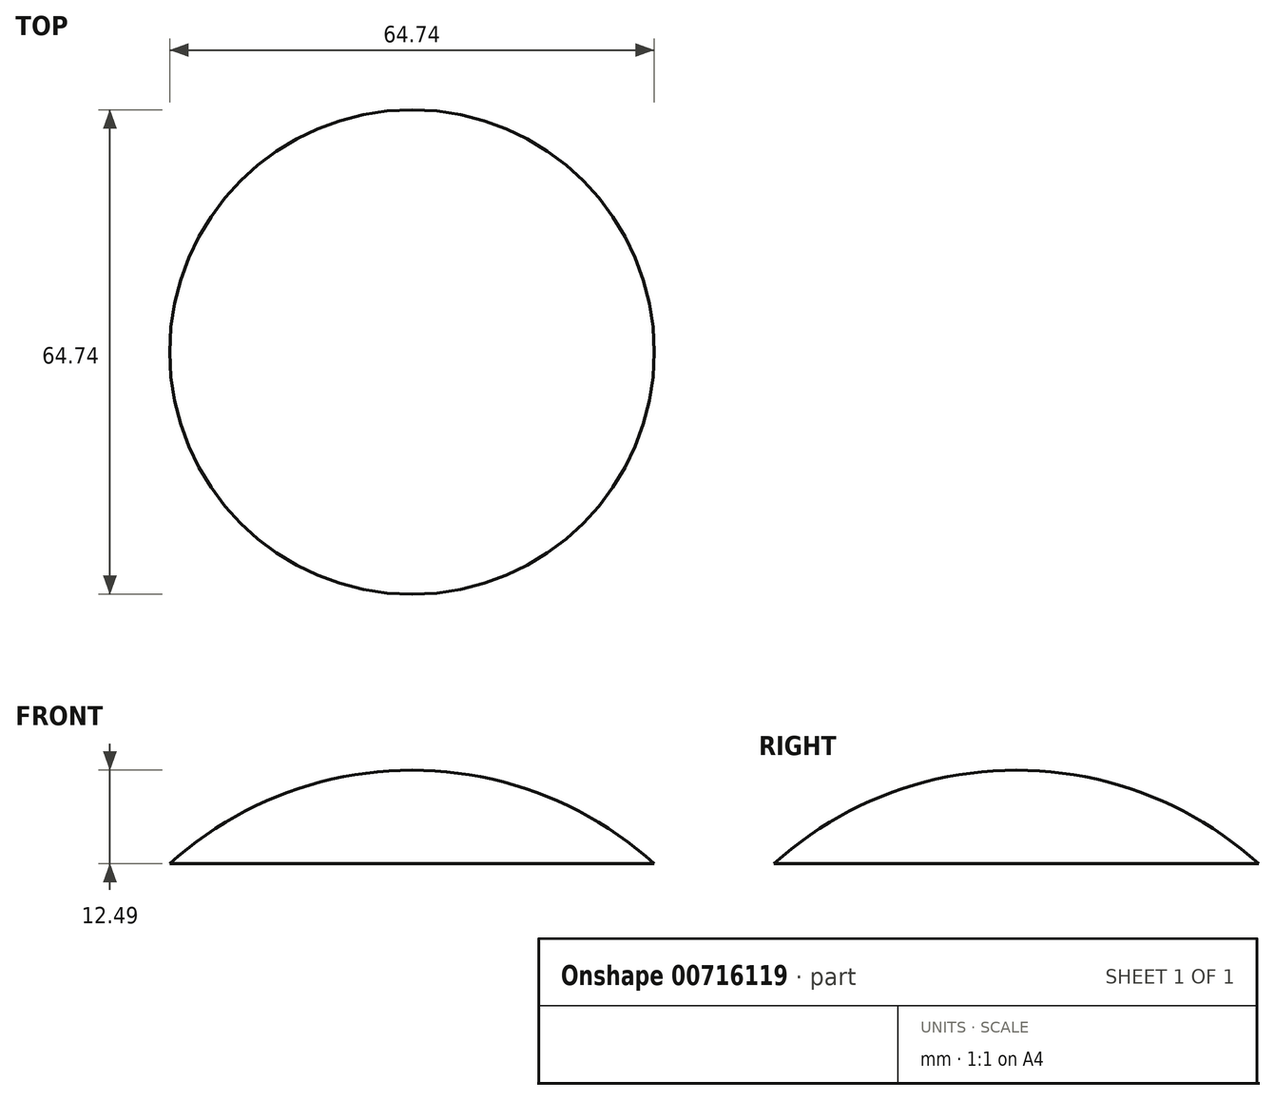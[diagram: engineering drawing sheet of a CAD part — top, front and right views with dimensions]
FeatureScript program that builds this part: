
annotation { "Feature Type Name" : "Feature", "Feature Type Description" : "" }
export const myFeature = defineFeature(function(context is Context, id is Id, definition is map)
    precondition{}
    {
        {
            var Q0;
            Q0=qCreatedBy(makeId("Front.planeOp"),FACE);
            var sketch = newSketch(context, id + "F0", { "sketchPlane" : qUnion([Q0])});
            skArc(sketch, "E0", {"start": v(32.37, 0) * mm, "mid": v(17.34, 9.25) * mm, "end": v(0, 12.5) * mm});
            skLineSegment(sketch, "E1", {"start": v(0, 12.5) * mm, "end": v(0, 0) * mm});
            skLineSegment(sketch, "E2", {"start": v(0, 0) * mm, "end": v(32.37, 0) * mm});
            skSolve(sketch);
        }
        {
            var Q0;
            Q0=makeQuery(id+"F0.imprint","IMPRINT",FACE,{"disambiguationData":[TD([[makeQuery(id+"F0.imprint","IMPRINT",EDGE,{"derivedFrom":sQuery(id+"F0.wireOp",EDGE,"E0")}),1.0]])]});
            var Q1;
            Q1=sQuery(id+"F0.wireOp",EDGE,"E1");
            revolve(context, id + "F1", {"surfaceOperationType" : NewSurfaceOperationType.NEW, "entities" : qUnion([Q0]), "axis" : qUnion([Q1]), "revolveType" : RevolveType.FULL});
        }
    });
